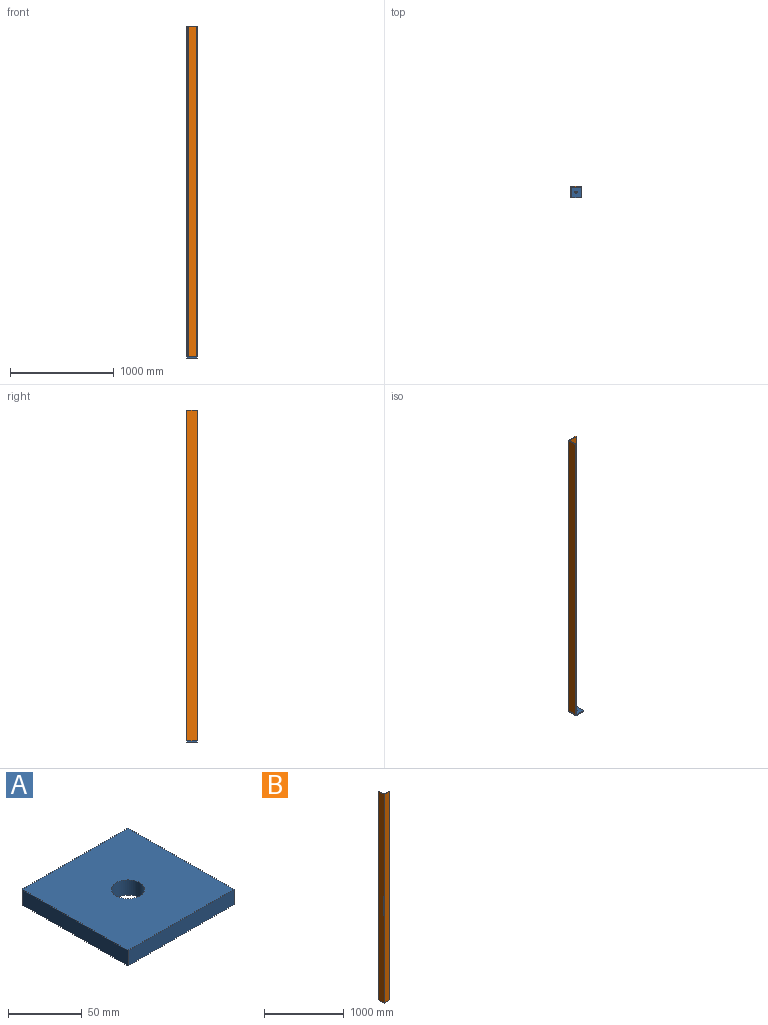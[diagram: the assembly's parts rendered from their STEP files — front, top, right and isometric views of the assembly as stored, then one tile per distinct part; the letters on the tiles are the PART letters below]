
ASSEMBLY  parts=2 mates=1
PART A: 7 faces, bbox 101.6x101.6x12.7 mm
  f0: plane 101.6x101.6mm, normal (0,0,-1), area 9934.6mm2, adj f1,f2,f3,f4,f5
  f1: plane 101.6x12.7mm, normal (-1,0,0), area 1290.3mm2, adj f0,f2,f4,f6
  f2: plane 101.6x12.7mm, normal (0,1,0), area 1290.3mm2, adj f0,f1,f3,f6
  f3: plane 101.6x12.7mm, normal (1,0,0), area 1290.3mm2, adj f0,f2,f4,f6
  f4: plane 101.6x12.7mm, normal (0,-1,0), area 1290.3mm2, adj f0,f1,f3,f6
  f5: cylinder r=11.11mm len=22.23mm, axis (0,0,1), area 886.7mm2, adj f0,f6
  f6: plane 101.6x101.6mm, normal (0,0,1), area 9934.6mm2, adj f1,f2,f3,f4,f5
PART B: 11 faces, bbox 101.6x101.6x3194.1 mm
  f0: plane 101.6x101.6mm, normal (0,0,1), area 1265.1mm2, adj f2,f3,f4,f5,f6,f7,f8,f9
  f1: plane 101.6x101.6mm, normal (0,0,-1), area 1265.1mm2, adj f2,f3,f4,f5,f6,f7,f8,f9
  f2: plane 3194.05x82.55mm, normal (1,0,0), area 263668.8mm2, adj f0,f1,f3,f10
  f3: cylinder r=9.52mm len=3194.05mm, axis (0,0,-1), area 47789.4mm2, adj f0,f1,f2,f4
  f4: plane 3194.05x82.55mm, normal (0,1,0), area 263668.8mm2, adj f0,f1,f3,f5
  f5: cylinder r=3.17mm len=3194.05mm, axis (0,0,-1), area 15929.8mm2, adj f0,f1,f4,f6
  f6: plane 3194.05x3.18mm, normal (1,0,0), area 10141.1mm2, adj f0,f1,f5,f7
  f7: plane 3194.05x101.6mm, normal (0,-1,0), area 324515.5mm2, adj f0,f1,f6,f8
  f8: plane 3194.05x101.6mm, normal (-1,0,0), area 324515.5mm2, adj f0,f1,f7,f9
  f9: plane 3194.05x3.18mm, normal (0,1,0), area 10141.1mm2, adj f0,f1,f8,f10
  f10: cylinder r=3.17mm len=3194.05mm, axis (0,0,-1), area 15929.8mm2, adj f0,f1,f2,f9
PLACE A rot(axis=(0,0,-1),90deg) t=(771.05,5113.66,-1187.52)mm
PLACE B rot(axis=(0,0,-1),90deg) t=(771.05,5113.66,-1187.52)mm
MATE fastened A.f6 <-> B.f1  axis (0,0,1) through (-143.35,5266.06,3632.13)mm
